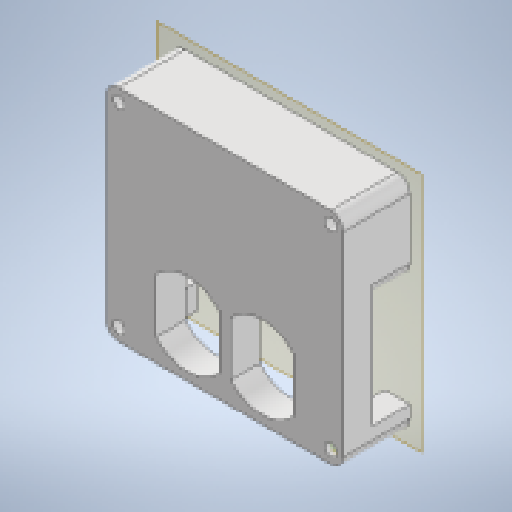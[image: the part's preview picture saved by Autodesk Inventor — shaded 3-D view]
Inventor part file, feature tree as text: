
AUTODESK INVENTOR PART (.ipt)
format: ipt  version: 2023 (Build 270158000, 158)  size: 279,040 bytes
history: native  units: mm
features: other x7, reference x4, plane x3, extrude x3, sketch x1, fillet x1
ambient origin geometry x8: Origin, YZ Plane, XZ Plane, XY Plane, X Axis, Y Axis, Z Axis, Center Point
bodies: Solid1 (feature_tree)
feature tree (19):
  plane  "Work Plane1"
  plane  "Work Plane2"
  plane  "Work Plane3"
  extrude  "Extrusion1"  TaperAngle=0.0deg  [1 undecoded]
  sketch  "Sketch4"  dims[d10=9.0mm d11=0.0mm d56=0.0mm d68=3.0mm d69=3.0mm d70=20.0mm d72=51.188mm d73=20.0mm d75=47.043mm d84=5.0mm d88=7.0mm d89=0.0mm d90=2.0mm d91=0.0mm d92=3.0mm d93=0.1mm d94=0.5mm d96=0.5mm d97=0.1mm d98=0.1mm d99=0.0mm d100=0.5mm d101=0.872665mm d102=0.5mm d103=0.872665mm]
  extrude  "Extrusion6"  Depth=3.0mm
  extrude  "Extrusion7"  Depth=3.0mm
  fillet  "Fillet2"  Radius=51.188mm
  reference  "Reference27"
  reference  "Reference28"
  reference  "Reference29"
  reference  "Reference30"
  parser-record x1  (decoder bookkeeping rows leaked as tree rows — omitted from the tree; the rows remain in map.json)
  other  "Assembly_V6.iam"
  other  "rack_V6:1"
  other  "motor:2"
  other  "motor:1"
  other  "mouldingPlate_V6:1"
  other  "screw:1"
note: 1 required parameter value undecoded (feature->parameter linkage not recoverable at this tier; creation-order binding heuristic only, values carry confidence <= 0.55)
note: 1 file-system path scrubbed to <path> (originals preserved in map.json)
